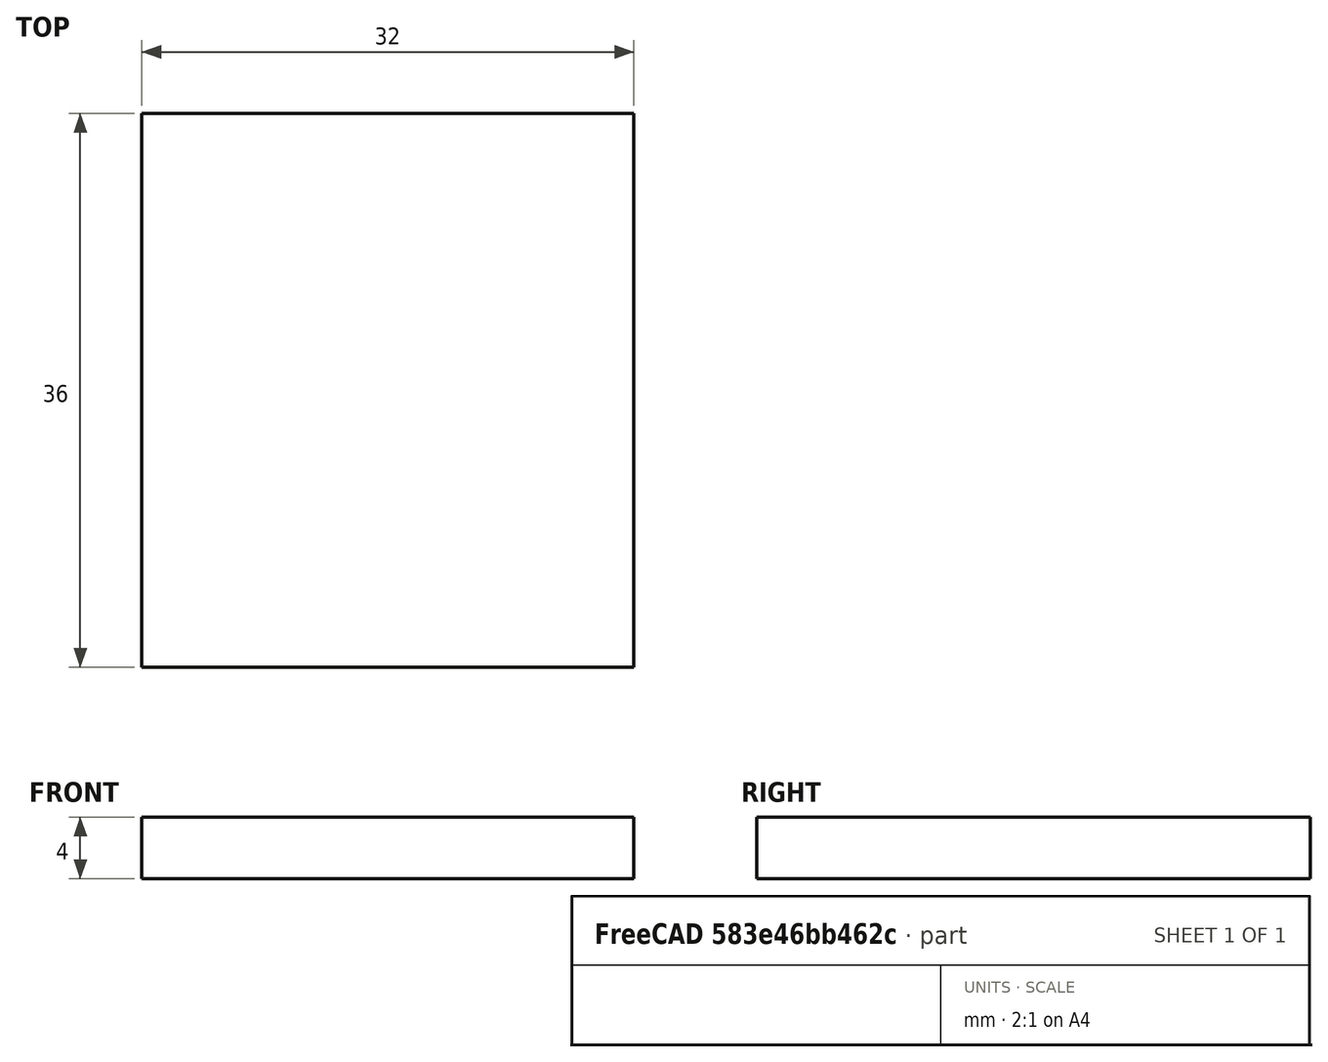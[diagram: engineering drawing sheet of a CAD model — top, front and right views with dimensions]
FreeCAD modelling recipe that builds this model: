
FCSTD DOCUMENT  (FreeCAD 1.0R39109 (Git))
Label: GPS_MOD13
License: All rights reserved
LicenseURL: http://en.wikipedia.org/wiki/All_rights_reserved
objects: Sketcher::SketchObject×1, PartDesign::Pad×1, PartDesign::Body×1
note: 6 computed .brp shape members not serialized (recipe doc carries the construction recipe); baked Part::Feature solids carry a one-line shape summary decoded from their .brp

FEATURE [Sketcher::SketchObject] Sketch
  ArcFitTolerance = 0
  AttachmentSupport = -> [XY_Plane]
  FullyConstrained = true
  MakeInternals = false
  MapMode = 5
  sketch-geometry (4):
    g0: LineSegment StartX=-16 StartY=18 StartZ=0 EndX=16 EndY=18 EndZ=0
    g1: LineSegment StartX=16 StartY=18 StartZ=0 EndX=16 EndY=-18 EndZ=0
    g2: LineSegment StartX=16 StartY=-18 StartZ=0 EndX=-16 EndY=-18 EndZ=0
    g3: LineSegment StartX=-16 StartY=-18 StartZ=0 EndX=-16 EndY=18 EndZ=0
  constraints (11):
    c: Coincident(g0,g1)
    c: Coincident(g1,g2)
    c: Coincident(g2,g3)
    c: Coincident(g3,g0)
    c: Horizontal(g0)
    c: Horizontal(g2)
    c: Vertical(g1)
    c: Vertical(g3)
    c: Symmetric(g0,g1,g-1)
    c: DistanceX(g0,g0) = 32
    c: DistanceY(g1,g1) = 36
FEATURE [PartDesign::Pad] Pad
  Direction = (0,0,1)
  Length = 4
  Length2 = 10
  Profile = -> Sketch
  ReferenceAxis = -> Sketch [N_Axis]
  Suppressed = false
  Type = 0
FEATURE [PartDesign::Body] Body  label="Corps"
  AllowCompound = false
  Group = -> [Sketch,Pad]
  Origin = -> Origin
  Tip = -> Pad
